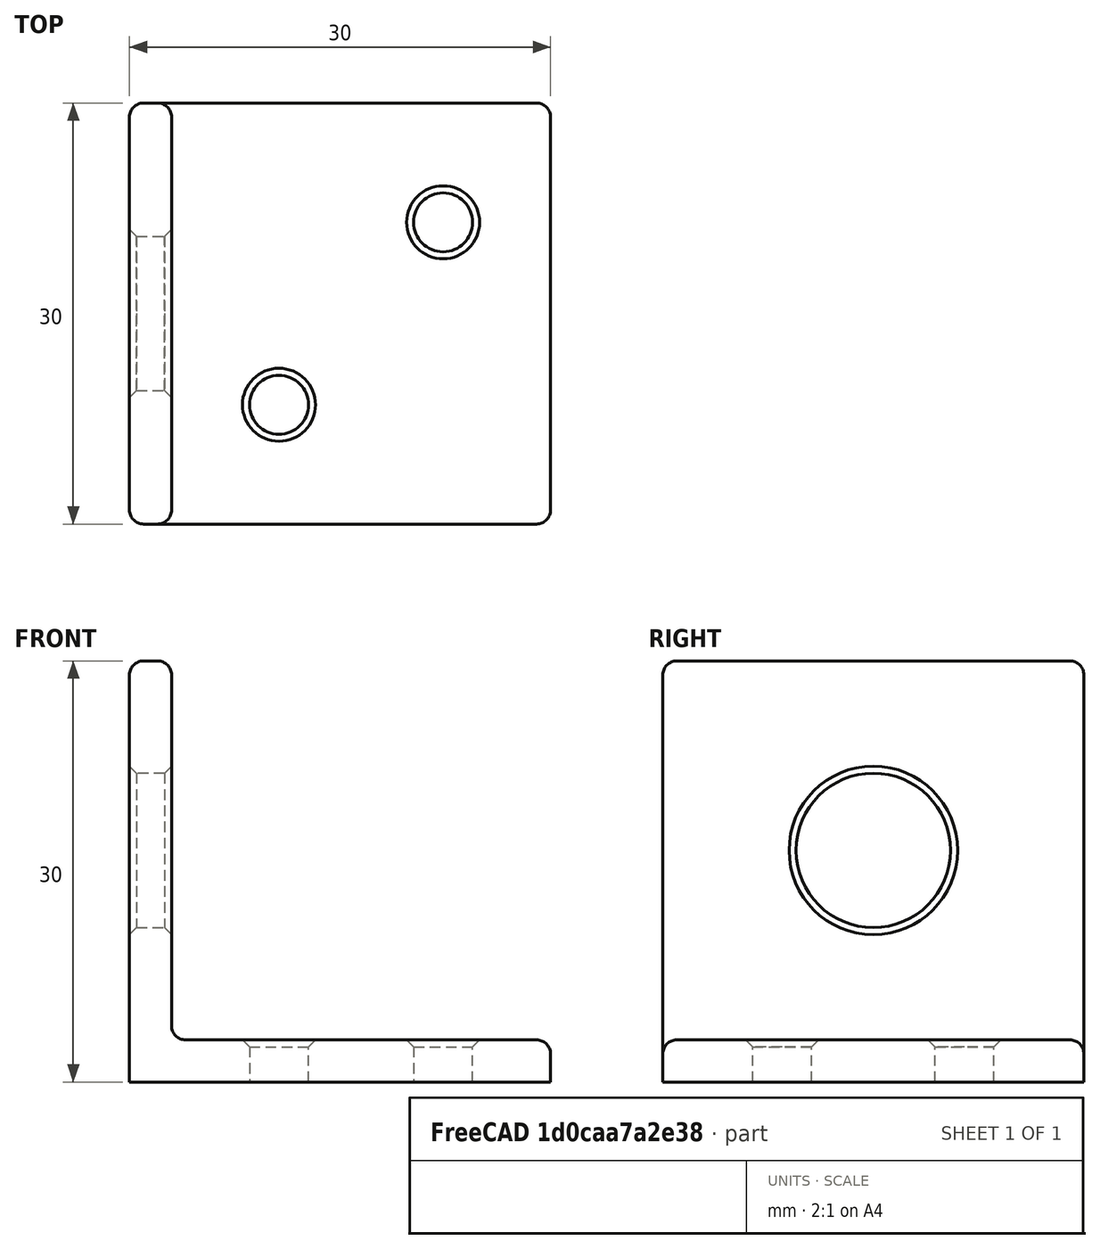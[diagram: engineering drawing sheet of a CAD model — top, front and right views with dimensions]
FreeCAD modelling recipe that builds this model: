
FCSTD DOCUMENT  (FreeCAD 0.19R24291 (Git))
Label: PowerMount_V1
License: All rights reserved
LicenseURL: http://en.wikipedia.org/wiki/All_rights_reserved
objects: Sketcher::SketchObject×3, PartDesign::Pocket×2, PartDesign::Pad×1, PartDesign::Fillet×1, PartDesign::Chamfer×1, PartDesign::Body×1, Mesh::Feature×1
note: 14 computed .brp shape members not serialized (recipe doc carries the construction recipe); baked Part::Feature solids carry a one-line shape summary decoded from their .brp

FEATURE [Sketcher::SketchObject] Sketch
  FullyConstrained = false
  MapMode = 5
  Placement = pos=(0,0,0) rot=(1,0,0;1.5708rad)
  Support = -> [XZ_Plane]
  sketch-geometry (6):
    g0: LineSegment StartX=0 StartY=0 StartZ=0 EndX=0 EndY=30 EndZ=0
    g1: LineSegment StartX=0 StartY=30 StartZ=0 EndX=3 EndY=30 EndZ=0
    g2: LineSegment StartX=3 StartY=30 StartZ=0 EndX=3 EndY=3 EndZ=0
    g3: LineSegment StartX=3 StartY=3 StartZ=0 EndX=30 EndY=3 EndZ=0
    g4: LineSegment StartX=30 StartY=3 StartZ=0 EndX=30 EndY=0 EndZ=0
    g5: LineSegment StartX=30 StartY=0 StartZ=0 EndX=0 EndY=0 EndZ=0
  constraints (17):
    c: Coincident(g-1,g0)
    c: PointOnObject(g0,g-2)
    c: Coincident(g0,g1)
    c: Horizontal(g1)
    c: Coincident(g1,g2)
    c: Vertical(g2)
    c: Coincident(g2,g3)
    c: Horizontal(g3)
    c: Coincident(g3,g4)
    c: PointOnObject(g4,g-1)
    c: Vertical(g4)
    c: Coincident(g4,g5)
    c: Coincident(g5,g0)
    c: Distance(g1) = 3
    c: Equal(g4,g1)
    c: Distance(g0) = 30
    c: Distance(g5) = 30
FEATURE [PartDesign::Pad] Pad
  Direction = (1,1,1)
  Length = 30
  Length2 = 100
  Placement = pos=(0,0,0) rot=(1,0,0;1.5708rad)
  Profile = -> Sketch
  Type = 0
FEATURE [Sketcher::SketchObject] Sketch001
  ExternalGeometry = -> [Pad]
  FullyConstrained = false
  MapMode = 5
  Placement = pos=(3,0,0) rot=(0.707107,0,0.707107;3.14159rad)
  Support = -> [Pad]
  expr: Constraints[6] = 11 / 2
  sketch-geometry (3):
    g0: Circle CenterX=16.5 CenterY=15 CenterZ=0 NormalX=0 NormalY=0 NormalZ=1 AngleXU=0 Radius=5.5
    g1: LineSegment StartX=3 StartY=-2e-15 StartZ=0 EndX=30 EndY=30 EndZ=0
    g2: LineSegment StartX=3 StartY=30 StartZ=0 EndX=30 EndY=-2.13e-14 EndZ=0
  constraints (7):
    c: Coincident(g1,g-5)
    c: Coincident(g1,g-4)
    c: Coincident(g2,g-3)
    c: Coincident(g2,g-5)
    c: PointOnObject(g0,g2)
    c: PointOnObject(g0,g1)
    c: Radius(g0) = 5.5
FEATURE [PartDesign::Pocket] Pocket
  BaseFeature = -> Pad
  Length = 5
  Length2 = 100
  Placement = pos=(0,0,0) rot=(1,0,0;1.5708rad)
  Profile = -> Sketch001
  Type = 1
FEATURE [Sketcher::SketchObject] Sketch002
  ExternalGeometry = -> [Pocket]
  FullyConstrained = false
  MapMode = 5
  Placement = pos=(0,2e-15,3) rot=(0,0,1;3.14159rad)
  Support = -> [Pocket]
  expr: Constraints[3] = 4.2 / 2
  expr: Constraints[5] = 11 / 2 + 3
  expr: Constraints[6] = 11 / 2 + 3
  expr: Constraints[9] = 11 / 2
  sketch-geometry (5):
    g0: LineSegment StartX=-3 StartY=30 StartZ=0 EndX=-30 EndY=0 EndZ=0
    g1: Circle CenterX=-10.65 CenterY=21.5 CenterZ=0 NormalX=0 NormalY=0 NormalZ=1 AngleXU=0 Radius=2.1
    g2: Circle CenterX=-22.35 CenterY=8.5 CenterZ=0 NormalX=0 NormalY=0 NormalZ=1 AngleXU=0 Radius=2.1
    g3: Circle CenterX=-22.35 CenterY=8.5 CenterZ=0 NormalX=0 NormalY=0 NormalZ=1 AngleXU=0 Radius=5.5
    g4: Circle CenterX=-10.65 CenterY=21.5 CenterZ=0 NormalX=0 NormalY=0 NormalZ=1 AngleXU=0 Radius=5.5
  constraints (12):
    c: Coincident(g0,g-5)
    c: PointOnObject(g1,g0)
    c: PointOnObject(g2,g0)
    c: Radius(g1) = 2.1
    c: Equal(g1,g2)
    c: Distance(g2,g-5) = 8.5
    c: Distance(g1,g-3) = 8.5
    c: Coincident(g3,g2)
    c: Coincident(g4,g1)
    c: Radius(g4) = 5.5
    c: Equal(g4,g3)
    c: Coincident(g0,g-3)
FEATURE [PartDesign::Pocket] Pocket001
  BaseFeature = -> Pocket
  Length = 5
  Length2 = 100
  Placement = pos=(0,0,0) rot=(1,0,0;1.5708rad)
  Profile = -> Sketch002
  Type = 1
FEATURE [PartDesign::Fillet] Fillet
  Base = -> Pocket001 [Edge3,Edge16,Edge15,Edge17,Edge18,Edge22,Edge14,Edge19,Edge4,Edge2,Edge27,Edge12,Edge13,Edge11]
  BaseFeature = -> Pocket001
  Placement = pos=(0,0,0) rot=(1,0,0;1.5708rad)
  Radius = 1
  SupportTransform = false
FEATURE [PartDesign::Chamfer] Chamfer
  Angle = 45
  Base = -> Fillet [Edge22,Edge39,Edge41,Edge5]
  BaseFeature = -> Fillet
  ChamferType = 0
  FlipDirection = false
  Placement = pos=(0,0,0) rot=(1,0,0;1.5708rad)
  Size = 0.5
  Size2 = 1
  SupportTransform = false
FEATURE [PartDesign::Body] Body
  Group = -> [Sketch,Pad,Sketch001,Pocket,Sketch002,Pocket001,Fillet,Chamfer]
  Origin = -> Origin
  Tip = -> Chamfer
FEATURE [Mesh::Feature] Mesh  label="Chamfer (Meshed)"
